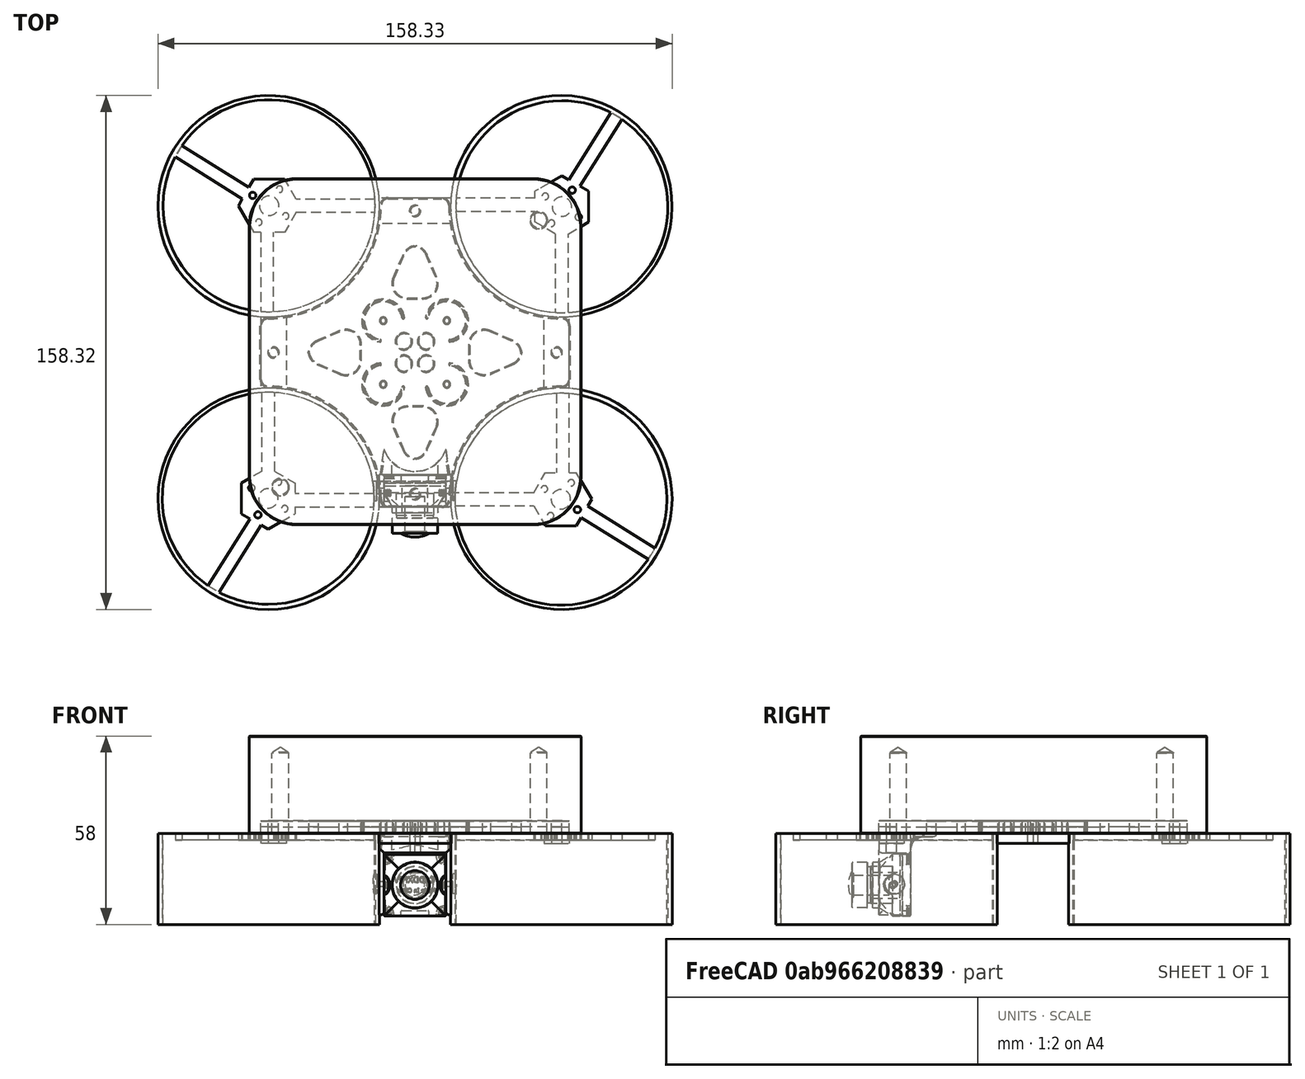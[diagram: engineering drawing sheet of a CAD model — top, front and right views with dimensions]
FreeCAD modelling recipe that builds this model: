
FCSTD DOCUMENT  (FreeCAD 1.1RUnknown)
Label: frame
License: All rights reserved
LicenseURL: http://en.wikipedia.org/wiki/All_rights_reserved
objects: Sketcher::SketchObject×17, PartDesign::SubShapeBinder×11, PartDesign::Pad×10, App::Point×5, PartDesign::Pocket×5, PartDesign::Body×5, PartDesign::Fillet×4, PartDesign::Mirrored×3, PartDesign::Hole×3, Part::Feature×2, Part::DatumPlane×2, Mesh::Feature×1, PartDesign::Chamfer×1, PartDesign::PolarPattern×1
note: 129 computed .brp shape members not serialized (recipe doc carries the construction recipe); baked Part::Feature solids carry a one-line shape summary decoded from their .brp

FEATURE [Mesh::Feature] bottom
FEATURE [Part::Feature] bottom001
  shape: bbox 94.96 x 95.06 x 2.45 mm, 2172 faces, 0 solids (baked)
FEATURE [Sketcher::SketchObject] Sketch
  ArcFitTolerance = 1e-06
  ExternalGeometry = -> [bottom001]
  ExternalTypes = [0,0,0,0,0,0,0,0,0,0,0,0,0,0,0,0,0,0,0]
  FullyConstrained = false
  MakeInternals = false
  sketch-geometry (35):
    g0: Circle [constr] CenterX=51.281 CenterY=31.7129 CenterZ=0 NormalX=0 NormalY=0 NormalZ=1 AngleXU=0 Radius=0.98
    g1: Circle [constr] CenterX=51.281 CenterY=51.3129 CenterZ=0 NormalX=0 NormalY=0 NormalZ=1 AngleXU=0 Radius=0.98
    g2: LineSegment [constr] StartX=-6 StartY=41.53 StartZ=0 EndX=88.962 EndY=41.53 EndZ=0
    g3: LineSegment [constr] StartX=88.962 StartY=49.8447 StartZ=0 EndX=88.962 EndY=33.2153 EndZ=0
    g4: LineSegment [constr] StartX=51.281 StartY=51.3129 StartZ=0 EndX=51.281 EndY=31.7129 EndZ=0
    g5: GeomPoint [constr] X=51.281 Y=41.53 Z=0
    g6: LineSegment [constr] StartX=51.281 StartY=89.06 StartZ=0 EndX=51.281 EndY=-8.95995 EndZ=0
    g7: LineSegment [constr] StartX=51.281 StartY=51.3129 StartZ=0 EndX=88.962 EndY=51.3129 EndZ=0
    g8: LineSegment [constr] StartX=51.281 StartY=31.7129 StartZ=0 EndX=88.962 EndY=31.7129 EndZ=0
    g9: LineSegment [constr] StartX=88.962 StartY=51.3129 StartZ=0 EndX=88.962 EndY=31.7129 EndZ=0
    g10: LineSegment [constr] StartX=41.481 StartY=89.06 StartZ=0 EndX=41.481 EndY=-13.0957 EndZ=0
    g11: GeomPoint [constr] X=41.481 Y=41.53 Z=0
    g12: LineSegment [constr] StartX=41.481 StartY=41.53 StartZ=0 EndX=88.962 EndY=41.53 EndZ=0
    g13: LineSegment [constr] StartX=88.962 StartY=41.53 StartZ=0 EndX=88.8951 EndY=48.4597 EndZ=0
    g14: LineSegment StartX=49.7388 StartY=89.06 StartZ=0 EndX=41.481 EndY=89.06 EndZ=0
    g15: LineSegment [constr] StartX=41.481 StartY=89.06 StartZ=0 EndX=41.481 EndY=41.53 EndZ=0
    g16: ArcOfCircle CenterX=49.7388 CenterY=86.7775 CenterZ=0 NormalX=0 NormalY=0 NormalZ=1 AngleXU=0 Radius=2.28248 StartAngle=6.28209 EndAngle=7.85398
    g17: LineSegment [constr] StartX=41.481 StartY=41.53 StartZ=0 EndX=69.212 EndY=69.261 EndZ=0
    g18: LineSegment [constr] StartX=41.481 StartY=41.53 StartZ=0 EndX=62.2347 EndY=62.2837 EndZ=0
    g19: ArcOfCircle CenterX=86.4023 CenterY=86.7373 CenterZ=0 NormalX=0 NormalY=0 NormalZ=1 AngleXU=0 Radius=34.381 StartAngle=3.1405 EndAngle=3.93287
    g20: Circle [constr] CenterX=41.481 CenterY=85.14 CenterZ=0 NormalX=0 NormalY=0 NormalZ=1 AngleXU=0 Radius=1.568
    g21: ArcOfCircle CenterX=41.4666 CenterY=85.1388 CenterZ=0 NormalX=0 NormalY=0 NormalZ=1 AngleXU=0 Radius=1.58246 StartAngle=4.72149 EndAngle=7.84488
    g22: LineSegment [constr] StartX=41.481 StartY=86.7212 StartZ=0 EndX=41.481 EndY=83.5564 EndZ=0
    g23: ArcOfCircle CenterX=41.0001 CenterY=69.8983 CenterZ=0 NormalX=0 NormalY=0 NormalZ=1 AngleXU=0 Radius=4.3878 StartAngle=0.322942 EndAngle=1.46098
    g24: LineSegment StartX=45.1611 StartY=71.2908 StartZ=0 EndX=47.9343 EndY=64.8997 EndZ=0
    g25: LineSegment StartX=43.7247 StartY=58.2122 StartZ=0 EndX=41.481 EndY=58.2122 EndZ=0
    g26: ArcOfCircle CenterX=43.8184 CenterY=62.7782 CenterZ=0 NormalX=0 NormalY=0 NormalZ=1 AngleXU=0 Radius=4.6305 StartAngle=5.73156 EndAngle=6.75912
    g27: ArcOfCircle CenterX=43.926 CenterY=62.712 CenterZ=0 NormalX=0 NormalY=0 NormalZ=1 AngleXU=0 Radius=4.50424 StartAngle=4.66769 EndAngle=5.73156
    g28: LineSegment StartX=41.481 StartY=41.53 StartZ=0 EndX=41.481 EndY=58.2122 EndZ=0
    g29: LineSegment StartX=41.481 StartY=74.2596 StartZ=0 EndX=41.481 EndY=83.5564 EndZ=0
    g30: LineSegment StartX=51.9654 StartY=52.0144 StartZ=0 EndX=62.2347 EndY=62.2837 EndZ=0
    g31: LineSegment StartX=41.481 StartY=86.7212 StartZ=0 EndX=41.481 EndY=89.06 EndZ=0
    g32: ArcOfCircle CenterX=51.281 CenterY=51.3129 CenterZ=0 NormalX=0 NormalY=0 NormalZ=1 AngleXU=0 Radius=0.98 StartAngle=1.5708 EndAngle=3.91468
    g33: LineSegment StartX=50.5796 StartY=50.6286 StartZ=0 EndX=41.481 EndY=41.53 EndZ=0
    g34: ArcOfCircle CenterX=51.281 CenterY=51.3129 CenterZ=0 NormalX=0 NormalY=0 NormalZ=1 AngleXU=0 Radius=0.98 StartAngle=0.797712 EndAngle=1.5708
  constraints (82):
    c: PointOnObject(g-3,g0)
    c: PointOnObject(g-4,g0)
    c: PointOnObject(g-9,g1)
    c: PointOnObject(g-8,g1)
    c: PointOnObject(g-7,g1)
    c: Diameter(g1) = 1.96
    c: Diameter(g0) = 1.96
    c: Coincident(g2,g-11)
    c: Horizontal(g2)
    c: Coincident(g3,g-14)
    c: Coincident(g3,g-14)
    c: PointOnObject(g2,g3)
    c: Coincident(g4,g1)
    c: Coincident(g4,g0)
    c: PointOnObject(g5,g2)
    c: PointOnObject(g5,g4)
    c: PointOnObject(g-5,g0)
    c: Vertical(g6)
    c: PointOnObject(g0,g6)
    c: Coincident(g7,g1)
    c: Horizontal(g7)
    c: Coincident(g8,g0)
    c: Horizontal(g8)
    c: Coincident(g9,g7)
    c: Coincident(g9,g8)
    c: Vertical(g9)
    c: PointOnObject(g3,g9)
    c: DistanceY(g0,g1) = 19.6
    c: Coincident(g10,g-16)
    c: Vertical(g10)
    c: Symmetric(g2,g2,g11)
    c: Coincident(g12,g11)
    c: Coincident(g12,g2)
    c: Coincident(g12,g13)
    c: Coincident(g14,g10)
    c: Coincident(g14,g15)
    c: Coincident(g15,g12)
    c: Tangent(g14,g16) = -1.5708
    c: Block(g16)
    c: Coincident(g17,g11)
    c: Angle(g12,g17) = 0.785398
    c: Coincident(g18,g11)
    c: PointOnObject(g18,g17)
    c: Tangent(g19,g16) = 1.5708
    c: Coincident(g18,g19)
    c: PointOnObject(g20,g15)
    c: PointOnObject(g-18,g20)
    c: PointOnObject(g-17,g20)
    c: PointOnObject(g21,g15)
    c: PointOnObject(g21,g15)
    c: Tangent(g21,g20)
    c: Coincident(g22,g21)
    c: Coincident(g22,g21)
    c: PointOnObject(g23,g15)
    c: Coincident(g23,g-19)
    c: Coincident(g24,g23)
    c: PointOnObject(g25,g15)
    c: Horizontal(g25)
    c: Coincident(g24,g-21)
    c: Coincident(g26,g24)
    c: Coincident(g27,g25)
    c: PointOnObject(g-20,g27)
    c: Tangent(g27,g26) = -1.5708
    c: Coincident(g28,g11)
    c: Coincident(g28,g25)
    c: Coincident(g29,g23)
    c: Coincident(g29,g21)
    c: Coincident(g30,g18)
    c: Coincident(g31,g21)
    c: Coincident(g31,g10)
    c: PointOnObject(g32,g6)
    c: PointOnObject(g32,g17)
    c: PointOnObject(g-7,g32)
    c: Equal(g32,g1)
    c: PointOnObject(g32,g1)
    c: Coincident(g33,g32)
    c: Coincident(g33,g11)
    c: PointOnObject(g30,g17)
    c: PointOnObject(g30,g1)
    c: Coincident(g34,g32)
    c: Coincident(g34,g30)
    c: Tangent(g34,g1)
FEATURE [App::Point] Origin001
  Role = Origin
FEATURE [PartDesign::SubShapeBinder] Binder
  BindCopyOnChange = 0
  BindMode = 0
  ClaimChildren = false
  Context = -> Body [Binder.]
  Fuse = false
  MakeFace = true
  OffsetFill = false
  OffsetIntersection = false
  OffsetJoinType = 0
  OffsetOpenResult = false
  PartialLoad = false
  Relative = true
  Support = -> [Sketch]
  _Version = 2
FEATURE [PartDesign::Pad] Pad
  Direction = (0,0,1)
  Length = 2
  Length2 = 10
  Profile = -> Binder
  Suppressed = false
  Type = 0
FEATURE [Sketcher::SketchObject] Sketch001
  ArcFitTolerance = 1e-06
  ExternalGeometry = -> [Binder]
  ExternalTypes = [0]
  FullyConstrained = false
  MakeInternals = false
  MapMode = 5
  Placement = pos=(0,0,2.5) rot=(0,0,1;0rad)
  sketch-geometry (6):
    g0: ArcOfCircle CenterX=51.281 CenterY=51.3129 CenterZ=0 NormalX=0 NormalY=0 NormalZ=1 AngleXU=0 Radius=6.5 StartAngle=0.787255 EndAngle=2.97698
    g1: ArcOfCircle CenterX=51.281 CenterY=51.3129 CenterZ=0 NormalX=0 NormalY=0 NormalZ=1 AngleXU=0 Radius=6 StartAngle=0.787409 EndAngle=2.97698
    g2: ArcOfCircle CenterX=45.1155 CenterY=52.3371 CenterZ=0 NormalX=0 NormalY=0 NormalZ=1 AngleXU=0 Radius=0.25 StartAngle=2.97698 EndAngle=6.11858
    g3: LineSegment StartX=55.5151 StartY=55.5641 StartZ=0 EndX=55.8687 EndY=55.9177 EndZ=0
    g4: ArcOfCircle CenterX=44.9101 CenterY=44.9591 CenterZ=0 NormalX=0 NormalY=0 NormalZ=1 AngleXU=0 Radius=2.5 StartAngle=0.785398 EndAngle=3.92699
    g5: LineSegment StartX=43.1424 StartY=43.1914 StartZ=0 EndX=46.6779 EndY=46.7269 EndZ=0
  constraints (16):
    c: Tangent(g2,g1) = 1.5708
    c: Tangent(g2,g0) = -1.5708
    c: Coincident(g3,g1)
    c: Coincident(g3,g0)
    c: Distance(g3,g3) = 0.5
    c: Coincident(g0,g1)
    c: Distance(g0,g1) = 6
    c: PointOnObject(g0,g-3)
    c: PointOnObject(g1,g-3)
    c: Coincident(g0,g-18)
    c: PointOnObject(g4,g-16)
    c: PointOnObject(g4,g-16)
    c: Radius(g4) = 2.5
    c: Angle(g4) = 3.14159
    c: Coincident(g5,g4)
    c: Coincident(g5,g4)
FEATURE [Sketcher::SketchObject] Sketch002
  ArcFitTolerance = 1e-06
  ExternalGeometry = -> [Binder]
  ExternalTypes = [0]
  FullyConstrained = true
  MakeInternals = false
  MapMode = 5
  Placement = pos=(0,0,2.5) rot=(0,0,1;0rad)
  sketch-geometry (2):
    g0: LineSegment [constr] StartX=41.481 StartY=41.53 StartZ=0 EndX=41.481 EndY=0 EndZ=0
    g1: LineSegment [constr] StartX=41.481 StartY=41.53 StartZ=0 EndX=0 EndY=41.53 EndZ=0
  constraints (8):
    c: Coincident(g0,g-16)
    c: PointOnObject(g0,g-1)
    c: Vertical(g0)
    c: DistanceY(g0,g0) = 41.53  'd'
    c: Coincident(g1,g0)
    c: PointOnObject(g1,g-2)
    c: Horizontal(g1)
    c: DistanceX(g1,g1) = 41.481  'd2'
FEATURE [Sketcher::SketchObject] Sketch003
  ArcFitTolerance = 1e-06
  AttachmentSupport = -> [XZ_Plane]
  ExternalGeometry = -> [Binder]
  ExternalTypes = [0]
  FullyConstrained = false
  MakeInternals = false
  MapMode = 5
  Placement = pos=(0,0,0) rot=(1,0,0;1.5708rad)
  sketch-geometry (1):
    g0: LineSegment StartX=41.481 StartY=0 StartZ=0 EndX=41.481 EndY=28.0906 EndZ=0
  constraints (2):
    c: Coincident(g0,g-3)
    c: Vertical(g0)
FEATURE [Sketcher::SketchObject] Sketch004
  ArcFitTolerance = 1e-06
  ExternalTypes = [0]
  FullyConstrained = false
  MakeInternals = false
  MapMode = 5
  Placement = pos=(41.481,41.53,-9.2e-15) rot=(1,0,0;1.5708rad)
  sketch-geometry (1):
    g0: LineSegment StartX=0 StartY=1.01324 StartZ=0 EndX=0 EndY=32.8937 EndZ=0
  constraints (2):
    c: PointOnObject(g0,g-2)
    c: PointOnObject(g0,g-2)
FEATURE [PartDesign::Pocket] Pocket
  BaseFeature = -> Pad
  Direction = (0,0,-1)
  Length = 5
  Length2 = 5
  Profile = -> Sketch001
  ReferenceAxis = -> Sketch001 [N_Axis]
  Suppressed = false
  Type = 1
FEATURE [PartDesign::Mirrored] Mirrored
  BaseFeature = -> Pocket
  MirrorPlane = -> Pocket [Face10]
  Originals = -> [Pocket]
  Suppressed = false
  TransformMode = 1
FEATURE [PartDesign::Mirrored] Mirrored001
  BaseFeature = -> Mirrored
  MirrorPlane = -> Mirrored [Face27]
  Originals = -> [Mirrored]
  Suppressed = false
  TransformMode = 1
FEATURE [PartDesign::Mirrored] Mirrored002
  BaseFeature = -> Mirrored001
  MirrorPlane = -> Mirrored001 [Face24]
  Originals = -> [Mirrored001]
  Refine = true
  Suppressed = false
  TransformMode = 1
FEATURE [PartDesign::Body] Body  label="bottom plate"
  AllowCompound = false
  Group = -> [Binder,Pad,Sketch001,Sketch002,Sketch003,Sketch004,Pocket,Mirrored,Mirrored001,Mirrored002]
  Origin = -> Origin
  Tip = -> Mirrored002
FEATURE [App::Point] Origin003
  Role = Origin
FEATURE [PartDesign::SubShapeBinder] Binder001
  BindCopyOnChange = 0
  BindMode = 0
  ClaimChildren = false
  Context = -> Body001 [Binder001.]
  Fuse = false
  MakeFace = true
  OffsetFill = false
  OffsetIntersection = false
  OffsetJoinType = 0
  OffsetOpenResult = false
  PartialLoad = false
  Relative = true
  Support = -> [Body]
  _Version = 2
FEATURE [Sketcher::SketchObject] Sketch005
  ArcFitTolerance = 1e-06
  AttachmentSupport = -> [XY_Plane001]
  ExternalTypes = [0]
  FullyConstrained = false
  MakeInternals = false
  MapMode = 5
  sketch-geometry (10):
    g0: LineSegment StartX=-9.59007 StartY=80.3505 StartZ=0 EndX=-9.59007 EndY=3.20138 EndZ=0
    g1: LineSegment StartX=5.13409 StartY=-11.5228 StartZ=0 EndX=77.9266 EndY=-11.5228 EndZ=0
    g2: LineSegment StartX=92.6508 StartY=3.20138 StartZ=0 EndX=92.6508 EndY=80.3505 EndZ=0
    g3: LineSegment StartX=77.9266 StartY=95.0747 StartZ=0 EndX=5.13409 EndY=95.0747 EndZ=0
    g4: ArcOfCircle CenterX=5.13409 CenterY=80.3505 CenterZ=0 NormalX=0 NormalY=0 NormalZ=1 AngleXU=0 Radius=14.7242 StartAngle=1.5708 EndAngle=3.14159
    g5: ArcOfCircle CenterX=5.13409 CenterY=3.20138 CenterZ=0 NormalX=0 NormalY=0 NormalZ=1 AngleXU=0 Radius=14.7242 StartAngle=3.14159 EndAngle=4.71239
    g6: ArcOfCircle CenterX=77.9266 CenterY=3.20138 CenterZ=0 NormalX=0 NormalY=0 NormalZ=1 AngleXU=0 Radius=14.7242 StartAngle=4.71239 EndAngle=6.28319
    g7: ArcOfCircle CenterX=77.9266 CenterY=80.3505 CenterZ=0 NormalX=0 NormalY=0 NormalZ=1 AngleXU=0 Radius=14.7242 StartAngle=1e-16 EndAngle=1.5708
    g8: GeomPoint [constr] X=-9.59007 Y=95.0747 Z=0
    g9: GeomPoint [constr] X=92.6508 Y=-11.5228 Z=0
  constraints (19):
    c: Tangent(g0,g4) = -1.5708
    c: Tangent(g0,g5) = -1.5708
    c: Tangent(g1,g5) = -1.5708
    c: Tangent(g1,g6) = -1.5708
    c: Tangent(g2,g6) = -1.5708
    c: Tangent(g2,g7) = -1.5708
    c: Tangent(g3,g7) = -1.5708
    c: Tangent(g3,g4) = -1.5708
    c: Vertical(g0)
    c: Vertical(g2)
    c: Horizontal(g1)
    c: Horizontal(g3)
    c: Equal(g4,g5)
    c: Equal(g5,g6)
    c: Equal(g6,g7)
    c: PointOnObject(g8,g0)
    c: PointOnObject(g8,g3)
    c: PointOnObject(g9,g1)
    c: PointOnObject(g9,g2)
FEATURE [PartDesign::SubShapeBinder] Binder002
  BindCopyOnChange = 0
  BindMode = 0
  ClaimChildren = false
  Context = -> Body001 [Binder002.]
  Fuse = false
  MakeFace = true
  Offset = -0.25
  OffsetFill = false
  OffsetIntersection = false
  OffsetJoinType = 0
  OffsetOpenResult = false
  PartialLoad = false
  Relative = true
  Support = -> [Body[Mirrored002.Face84]]
  _Version = 2
FEATURE [PartDesign::Pad] Pad001
  Direction = (0,0,1)
  Length = 10
  Length2 = 10
  Profile = -> Sketch005
  ReferenceAxis = -> Sketch005 [N_Axis]
  Reversed = true
  Suppressed = false
  Type = 0
FEATURE [PartDesign::Pad] Pad002
  BaseFeature = -> Pad001
  Direction = (0,0,1)
  Length = 10
  Length2 = 10
  Profile = -> Binder002
  Reversed = true
  Suppressed = false
  Type = 0
FEATURE [App::Point] Origin005
  Role = Origin
FEATURE [PartDesign::SubShapeBinder] Binder004
  BindCopyOnChange = 0
  BindMode = 0
  ClaimChildren = false
  Context = -> Body002 [Binder004.]
  Fuse = false
  MakeFace = true
  OffsetFill = false
  OffsetIntersection = false
  OffsetJoinType = 0
  OffsetOpenResult = false
  PartialLoad = false
  Relative = true
  Support = -> [Body001[Sketch005.]]
  _Version = 2
FEATURE [PartDesign::Pad] Pad003
  Direction = (0,0,1)
  Length = 30
  Length2 = 10
  Profile = -> Binder004
  Reversed = true
  Suppressed = false
  Type = 0
FEATURE [PartDesign::SubShapeBinder] Binder005
  BindCopyOnChange = 0
  BindMode = 0
  ClaimChildren = false
  Context = -> Body002 [Binder005.]
  Fuse = false
  MakeFace = true
  OffsetFill = false
  OffsetIntersection = false
  OffsetJoinType = 0
  OffsetOpenResult = false
  PartialLoad = false
  Relative = true
  Support = -> [Body[Mirrored002.Face5]]
  _Version = 2
FEATURE [PartDesign::Pocket] Pocket001
  BaseFeature = -> Pad003
  Direction = (0,1e-16,-1)
  Length = 4
  Length2 = 5
  Profile = -> Binder005
  Suppressed = false
  Type = 0
FEATURE [Sketcher::SketchObject] Sketch006
  ArcFitTolerance = 1e-06
  AttachmentSupport = -> [Pad002]
  ExternalTypes = [0]
  FullyConstrained = false
  MakeInternals = false
  MapMode = 5
  sketch-geometry (2):
    g0: Circle CenterX=0 CenterY=0 CenterZ=0 NormalX=0 NormalY=0 NormalZ=1 AngleXU=0 Radius=3.5
    g1: Circle CenterX=79.5784 CenterY=82.2311 CenterZ=0 NormalX=0 NormalY=0 NormalZ=1 AngleXU=0 Radius=3.5
  constraints (3):
    c: Coincident(g0,g-1)
    c: Equal(g1,g0)
    c: Diameter(g1) = 7
FEATURE [PartDesign::Pad] Pad004
  BaseFeature = -> Pad002
  Direction = (0,0,1)
  Length = 5
  Length2 = 10
  Profile = -> Sketch006
  ReferenceAxis = -> Sketch006 [N_Axis]
  Suppressed = false
  Type = 0
FEATURE [PartDesign::SubShapeBinder] Binder006
  BindCopyOnChange = 0
  BindMode = 0
  ClaimChildren = false
  Context = -> Body002 [Binder006.]
  Fuse = false
  MakeFace = true
  OffsetFill = false
  OffsetIntersection = false
  OffsetJoinType = 0
  OffsetOpenResult = false
  PartialLoad = false
  Relative = true
  Support = -> [Body001[Sketch006.]]
  _Version = 2
FEATURE [PartDesign::Hole] Hole
  BaseFeature = -> Pocket001
  CustomThreadClearance = 0
  Depth = 25
  DepthType = 0
  Diameter = 5.1
  DrillForDepth = false
  DrillPoint = 1
  DrillPointAngle = 118
  HoleCutCountersinkAngle = 90
  HoleCutCustomValues = false
  HoleCutDepth = 0
  HoleCutDiameter = 6.1
  HoleCutType = 0
  ModelThread = false
  Profile = -> Binder006
  Suppressed = false
  Tapered = false
  TaperedAngle = 90
  ThreadClass = 0
  ThreadDepth = 25
  ThreadDepthType = 0
  ThreadDirection = 0
  ThreadFit = 0
  ThreadSize = 0
  ThreadType = 0
  Threaded = false
  UseCustomThreadClearance = false
FEATURE [PartDesign::Chamfer] Chamfer
  Angle = 45
  Base = -> Hole [Edge131,Edge142]
  BaseFeature = -> Hole
  ChamferType = 0
  FlipDirection = false
  Size = 0.18
  Size2 = 1
  SupportTransform = false
  Suppressed = false
  UseAllEdges = true
FEATURE [PartDesign::Body] Body002
  AllowCompound = false
  Group = -> [Binder004,Pad003,Binder005,Pocket001,Binder006,Hole,Chamfer]
  Origin = -> Origin004
  Placement = pos=(0,-120.18,43.09) rot=(1,0,0;3.14159rad)
  Tip = -> Chamfer
FEATURE [PartDesign::Fillet] Fillet
  Base = -> Pad002 [Face31,Face138,Face139,Face137,Face136,Face4]
  BaseFeature = -> Pad002
  Radius = 0.18
  SupportTransform = false
  Suppressed = false
  UseAllEdges = false
FEATURE [PartDesign::Body] Body001  label="Body"
  AllowCompound = false
  Group = -> [Binder001,Sketch005,Binder002,Pad001,Pad002,Sketch006,Pad004,Fillet]
  Origin = -> Origin002
  Tip = -> Fillet
FEATURE [App::Point] Origin007
  Role = Origin
FEATURE [PartDesign::SubShapeBinder] Binder007
  BindCopyOnChange = 0
  BindMode = 0
  ClaimChildren = false
  Context = -> Body003 [Binder007.]
  Fuse = false
  MakeFace = true
  OffsetFill = false
  OffsetIntersection = false
  OffsetJoinType = 0
  OffsetOpenResult = false
  PartialLoad = false
  Relative = true
  Support = -> [Body]
  _Version = 2
FEATURE [Sketcher::SketchObject] Sketch007
  ArcFitTolerance = 1e-06
  AttachmentSupport = -> [XY_Plane003]
  ExternalGeometry = -> [Binder007]
  ExternalTypes = [0,0,0,0,0,0]
  FullyConstrained = true
  MakeInternals = false
  MapMode = 5
  sketch-geometry (5):
    g0: LineSegment [constr] StartX=86.4023 StartY=-3.67734 StartZ=0 EndX=86.6883 EndY=-3.39127 EndZ=0
    g1: GeomPoint [constr] X=86.5453 Y=-3.53431 Z=0
    g2: Circle [constr] CenterX=86.5453 CenterY=-3.53431 CenterZ=0 NormalX=0 NormalY=0 NormalZ=1 AngleXU=0 Radius=31.75
    g3: Circle CenterX=86.5453 CenterY=-3.53431 CenterZ=0 NormalX=0 NormalY=0 NormalZ=1 AngleXU=0 Radius=34.1
    g4: Circle CenterX=86.4023 CenterY=-3.67734 CenterZ=0 NormalX=0 NormalY=0 NormalZ=1 AngleXU=0 Radius=32.6477
  constraints (9):
    c: Coincident(g0,g-7)
    c: Coincident(g0,g-8)
    c: Symmetric(g0,g0,g1)
    c: Coincident(g2,g1)
    c: Diameter(g2) = 63.5
    c: Coincident(g3,g1)
    c: Distance(g3,g2) = 2.35
    c: Coincident(g4,g0)
    c: Distance(g4,g3) = 1.25
FEATURE [PartDesign::Pad] Pad005
  Direction = (0,0,1)
  Length = 0
  Length2 = 28
  Profile = -> Sketch007
  ReferenceAxis = -> Sketch007 [N_Axis]
  Suppressed = false
  Type = 4
FEATURE [Sketcher::SketchObject] Sketch008
  ArcFitTolerance = 1e-06
  AttachmentSupport = -> [Pad005]
  ExternalGeometry = -> [Binder007,Pad005]
  ExternalTypes = [0,0,0,0,0,0]
  FullyConstrained = true
  MakeInternals = false
  MapMode = 5
  sketch-geometry (12):
    g0: LineSegment StartX=89.011 StartY=28.866 StartZ=0 EndX=89.011 EndY=41.53 EndZ=0
    g1: LineSegment [constr] StartX=89.011 StartY=41.53 StartZ=0 EndX=81.1685 EndY=41.53 EndZ=0
    g2: LineSegment StartX=81.1685 StartY=41.53 StartZ=0 EndX=81.1685 EndY=29.8314 EndZ=0
    g3: ArcOfCircle CenterX=85.0898 CenterY=41.5444 CenterZ=0 NormalX=0 NormalY=0 NormalZ=1 AngleXU=0 Radius=1.58246 StartAngle=3.15069 EndAngle=6.27408
    g4: LineSegment StartX=81.1685 StartY=41.53 StartZ=0 EndX=83.5074 EndY=41.53 EndZ=0
    g5: LineSegment StartX=86.6722 StartY=41.53 StartZ=0 EndX=89.011 EndY=41.53 EndZ=0
    g6: LineSegment StartX=81.1685 StartY=29.8314 StartZ=0 EndX=89.011 EndY=28.866 EndZ=0
    g7: LineSegment StartX=41.481 StartY=-3.66116 StartZ=0 EndX=41.481 EndY=-6 EndZ=0
    g8: LineSegment StartX=41.481 StartY=-6 StartZ=0 EndX=53.8373 EndY=-6 EndZ=0
    g9: LineSegment StartX=53.8373 StartY=-6 StartZ=0 EndX=52.8719 EndY=1.84248 EndZ=0
    g10: LineSegment StartX=41.481 StartY=-0.496368 StartZ=0 EndX=41.481 EndY=1.84248 EndZ=0
    g11: LineSegment StartX=41.481 StartY=1.84248 StartZ=0 EndX=52.8719 EndY=1.84248 EndZ=0
  constraints (32):
    c: Coincident(g0,g1)
    c: Coincident(g1,g2)
    c: Horizontal(g1)
    c: Vertical(g0)
    c: Vertical(g2)
    c: PointOnObject(g-5,g0)
    c: PointOnObject(g-4,g1)
    c: Tangent(g3,g-4) = -1.5708
    c: Coincident(g3,g-4)
    c: Coincident(g4,g1)
    c: Coincident(g4,g-4)
    c: Coincident(g5,g3)
    c: Coincident(g5,g0)
    c: Coincident(g6,g2)
    c: Coincident(g6,g0)
    c: Coincident(g7,g-6)
    c: Vertical(g7)
    c: Coincident(g8,g7)
    c: Horizontal(g8)
    c: Coincident(g9,g8)
    c: Equal(g9,g6)
    c: Coincident(g10,g-6)
    c: Vertical(g10)
    c: Equal(g5,g7)
    c: Equal(g4,g10)
    c: Equal(g10,g7)
    c: Coincident(g11,g10)
    c: Coincident(g11,g9)
    c: Horizontal(g11)
    c: PointOnObject(g8,g-7)
    c: PointOnObject(g9,g-8)
    c: PointOnObject(g0,g-7)
FEATURE [PartDesign::Pad] Pad006
  BaseFeature = -> Pad005
  Direction = (0,0,1)
  Length = 3
  Length2 = 10
  Profile = -> Sketch008
  ReferenceAxis = -> Sketch008 [N_Axis]
  Reversed = true
  Suppressed = false
  Type = 0
FEATURE [Sketcher::SketchObject] Sketch009
  ArcFitTolerance = 1e-06
  AttachmentSupport = -> [XY_Plane003]
  ExternalGeometry = -> [Sketch008,Pad006]
  ExternalTypes = [0,0,0,0]
  FullyConstrained = false
  MakeInternals = false
  MapMode = 5
  sketch-geometry (36):
    g0: LineSegment [constr] StartX=91.1523 StartY=4.5499 StartZ=0 EndX=81.6523 EndY=4.5499 EndZ=0
    g1: LineSegment [constr] StartX=81.6523 StartY=4.5499 StartZ=0 EndX=76.9023 EndY=-3.67734 EndZ=0
    g2: LineSegment [constr] StartX=76.9023 StartY=-3.67734 StartZ=0 EndX=81.6523 EndY=-11.9046 EndZ=0
    g3: LineSegment StartX=81.6523 StartY=-11.9046 StartZ=0 EndX=91.1523 EndY=-11.9046 EndZ=0
    g4: LineSegment [constr] StartX=91.1523 StartY=-11.9046 StartZ=0 EndX=95.9023 EndY=-3.67734 EndZ=0
    g5: LineSegment StartX=95.9023 StartY=-3.67734 StartZ=0 EndX=91.1523 EndY=4.5499 EndZ=0
    g6: Circle [constr] CenterX=86.4023 CenterY=-3.67734 CenterZ=0 NormalX=0 NormalY=0 NormalZ=1 AngleXU=0 Radius=9.5
    g7: LineSegment [constr] StartX=95.9023 StartY=-3.67734 StartZ=0 EndX=76.9023 EndY=-3.67734 EndZ=0
    g8: LineSegment StartX=78.057 StartY=-1.67734 StartZ=0 EndX=53.8159 EndY=-1.67734 EndZ=0
    g9: LineSegment [constr] StartX=53.8159 StartY=-1.67734 StartZ=0 EndX=53.8159 EndY=-5.67734 EndZ=0
    g10: LineSegment StartX=53.8159 StartY=-5.67734 StartZ=0 EndX=78.057 EndY=-5.67734 EndZ=0
    g11: LineSegment [constr] StartX=78.057 StartY=-5.67734 StartZ=0 EndX=78.057 EndY=-1.67734 EndZ=0
    g12: LineSegment StartX=78.057 StartY=-1.67734 StartZ=0 EndX=81.6523 EndY=4.5499 EndZ=0
    g13: LineSegment StartX=78.057 StartY=-5.67734 StartZ=0 EndX=81.6523 EndY=-11.9046 EndZ=0
    g14: ArcOfCircle CenterX=55.6667 CenterY=-3.67734 CenterZ=0 NormalX=0 NormalY=0 NormalZ=1 AngleXU=0 Radius=2.725 StartAngle=2.31748 EndAngle=3.9657
    g15: LineSegment StartX=92.6685 StartY=-9.27845 StartZ=0 EndX=113.29 EndY=-22.1957 EndZ=0
    g16: LineSegment StartX=94.6685 StartY=-5.81435 StartZ=0 EndX=115.352 EndY=-18.7704 EndZ=0
    g17: ArcOfCircle CenterX=112.734 CenterY=-19.528 CenterZ=0 NormalX=0 NormalY=0 NormalZ=1 AngleXU=0 Radius=2.725 StartAngle=4.91775 EndAngle=6.56491
    g18: LineSegment StartX=91.1523 StartY=-11.9046 StartZ=0 EndX=92.6685 EndY=-9.27845 EndZ=0
    g19: LineSegment StartX=94.6685 StartY=-5.81435 StartZ=0 EndX=95.9023 EndY=-3.67734 EndZ=0
    g20: LineSegment [constr] StartX=85.011 StartY=4.5499 StartZ=0 EndX=89.011 EndY=4.5499 EndZ=0
    g21: LineSegment StartX=89.011 StartY=4.5499 StartZ=0 EndX=89.011 EndY=28.866 EndZ=0
    g22: LineSegment [constr] StartX=89.011 StartY=28.866 StartZ=0 EndX=85.011 EndY=28.866 EndZ=0
    g23: LineSegment StartX=85.011 StartY=28.866 StartZ=0 EndX=85.011 EndY=4.5499 EndZ=0
    g24: LineSegment StartX=81.6523 StartY=4.5499 StartZ=0 EndX=85.011 EndY=4.5499 EndZ=0
    g25: LineSegment StartX=89.011 StartY=4.5499 StartZ=0 EndX=91.1523 EndY=4.5499 EndZ=0
    g26: LineSegment [constr] StartX=89.011 StartY=28.866 StartZ=0 EndX=89.011 EndY=28.866 EndZ=0
    g27: ArcOfCircle CenterX=87.011 CenterY=27.0151 CenterZ=0 NormalX=0 NormalY=0 NormalZ=1 AngleXU=0 Radius=2.725 StartAngle=0.746684 EndAngle=2.39491
    g28: LineSegment [constr] StartX=86.4023 StartY=-3.67734 StartZ=0 EndX=114.07 EndY=-21.0084 EndZ=0
    g29: Circle CenterX=81.3175 CenterY=-0.492235 CenterZ=0 NormalX=0 NormalY=0 NormalZ=1 AngleXU=0 Radius=1
    g30: Circle CenterX=89.5874 CenterY=1.40744 CenterZ=0 NormalX=0 NormalY=0 NormalZ=1 AngleXU=0 Radius=1
    g31: Circle CenterX=91.4871 CenterY=-6.86245 CenterZ=0 NormalX=0 NormalY=0 NormalZ=1 AngleXU=0 Radius=1
    g32: Circle CenterX=83.2172 CenterY=-8.76213 CenterZ=0 NormalX=0 NormalY=0 NormalZ=1 AngleXU=0 Radius=1
    g33: LineSegment [constr] StartX=81.3175 StartY=-0.492235 StartZ=0 EndX=91.4871 EndY=-6.86245 EndZ=0
    g34: LineSegment [constr] StartX=89.5874 StartY=1.40744 StartZ=0 EndX=83.2172 EndY=-8.76213 EndZ=0
    g35: Circle CenterX=86.4023 CenterY=-3.67734 CenterZ=0 NormalX=0 NormalY=0 NormalZ=1 AngleXU=0 Radius=3
  constraints (92):
    c: Coincident(g0,g1)
    c: Coincident(g1,g2)
    c: Coincident(g2,g3)
    c: Coincident(g3,g4)
    c: Coincident(g4,g5)
    c: Coincident(g5,g0)
    c: Equal(g0, g1-g5) x5
    c: PointOnObject(g0,g6)
    c: PointOnObject(g1,g6)
    c: PointOnObject(g2,g6)
    c: PointOnObject(g3,g6)
    c: PointOnObject(g4,g6)
    c: PointOnObject(g5,g6)
    c: Coincident(g6,g-4)
    c: Diameter(g6) = 19
    c: Horizontal(g3)
    c: Coincident(g7,g4)
    c: PointOnObject(g7,g1)
    c: Horizontal(g7)
    c: Coincident(g8,g9)
    c: Coincident(g9,g10)
    c: Coincident(g10,g11)
    c: Coincident(g11,g8)
    c: Horizontal(g8)
    c: Horizontal(g10)
    c: Vertical(g9)
    c: Vertical(g11)
    c: PointOnObject(g8,g1)
    c: PointOnObject(g10,g2)
    c: Coincident(g12,g8)
    c: Coincident(g12,g0)
    c: Coincident(g13,g10)
    c: Coincident(g13,g2)
    c: PointOnObject(g8,g-5)
    c: DistanceY(g9,g9) = 4
    c: Coincident(g14,g8)
    c: Coincident(g14,g9)
    c: PointOnObject(g15,g4)
    c: PointOnObject(g15,g-5)
    c: PointOnObject(g16,g4)
    c: PointOnObject(g16,g-5)
    c: Coincident(g17,g16)
    c: Coincident(g17,g15)
    c: Coincident(g18,g3)
    c: Coincident(g18,g15)
    c: Coincident(g19,g16)
    c: Coincident(g19,g4)
    c: Equal(g17,g14)
    c: Radius(g14) = 2.725
    c: Parallel(g15,g16)
    c: Distance(g15,g16) = 4
    c: Coincident(g20,g21)
    c: Coincident(g21,g22)
    c: Coincident(g22,g23)
    c: Coincident(g23,g20)
    c: Horizontal(g20)
    c: Horizontal(g22)
    c: Vertical(g21)
    c: Vertical(g23)
    c: PointOnObject(g20,g0)
    c: PointOnObject(g21,g-4)
    c: DistanceX(g22,g22) = 4
    c: Coincident(g24,g0)
    c: Coincident(g24,g20)
    c: Coincident(g25,g20)
    c: Coincident(g25,g0)
    c: Coincident(g26,g-6)
    c: Coincident(g26,g21)
    c: Vertical(g26)
    c: Coincident(g27,g22)
    c: Coincident(g27,g21)
    c: Equal(g27,g17)
    c: Coincident(g28,g6)
    c: PointOnObject(g28,g-5)
    c: Parallel(g15,g28)
    c: Equal(g32,g31)
    c: Equal(g31,g30)
    c: Equal(g30,g29)
    c: Diameter(g29) = 2
    c: Coincident(g33,g29)
    c: Coincident(g33,g31)
    c: Distance(g33,g33) = 12
    c: Coincident(g34,g30)
    c: Coincident(g32,g34)
    c: Distance(g34,g34) = 12
    c: Symmetric(g32,g30,g33)
    c: Symmetric(g31,g29,g34)
    c: PointOnObject(g31,g28)
    c: PointOnObject(g6,g34)
    c: PointOnObject(g6,g33)
    c: Coincident(g35,g6)
    c: Diameter(g35) = 6
FEATURE [PartDesign::Pad] Pad007
  BaseFeature = -> Pad006
  Direction = (0,0,1)
  Length = 2
  Length2 = 10
  Profile = -> Sketch009
  ReferenceAxis = -> Sketch009 [N_Axis]
  Refine = true
  Reversed = true
  Suppressed = false
  Type = 0
FEATURE [PartDesign::SubShapeBinder] Binder008
  BindCopyOnChange = 0
  BindMode = 0
  ClaimChildren = false
  Context = -> Body003 [Binder008.]
  Fuse = false
  MakeFace = true
  OffsetFill = false
  OffsetIntersection = false
  OffsetJoinType = 0
  OffsetOpenResult = false
  PartialLoad = false
  Relative = true
  Support = -> [Body[Sketch004.]]
  _Version = 2
FEATURE [PartDesign::PolarPattern] PolarPattern
  Angle = 360
  Axis = -> Binder008 [Edge1]
  BaseFeature = -> Pad007
  Mode = 0
  Occurrences = 4
  Offset = 120
  Originals = -> [Pad007]
  Refine = true
  Suppressed = false
  TransformMode = 1
FEATURE [App::Point] Origin009
  Role = Origin
FEATURE [PartDesign::SubShapeBinder] Binder009
  BindCopyOnChange = 0
  BindMode = 0
  ClaimChildren = false
  Context = -> Body004 [Binder009.]
  Fuse = false
  MakeFace = true
  OffsetFill = false
  OffsetIntersection = false
  OffsetJoinType = 0
  OffsetOpenResult = false
  PartialLoad = false
  Relative = true
  Support = -> [Body]
  _Version = 2
FEATURE [Sketcher::SketchObject] Sketch010
  ArcFitTolerance = 1e-06
  AttachmentSupport = -> [XY_Plane004]
  ExternalGeometry = -> [Binder009]
  ExternalTypes = [0,0,0,0,0,0,0,0,0,0,0,0,0,0,0,0]
  FullyConstrained = false
  MakeInternals = false
  MapMode = 5
  sketch-geometry (7):
    g0: LineSegment StartX=30.4666 StartY=1.84248 StartZ=0 EndX=52.4666 EndY=1.84248 EndZ=0
    g1: LineSegment [constr] StartX=31.9666 StartY=34.7471 StartZ=0 EndX=53.9091 EndY=34.7471 EndZ=0
    g2: LineSegment [constr] StartX=41.4666 StartY=1.84248 StartZ=0 EndX=41.4666 EndY=34.7462 EndZ=0
    g3: ArcOfCircle CenterX=41.4666 CenterY=14.8425 CenterZ=0 NormalX=0 NormalY=0 NormalZ=1 AngleXU=0 Radius=10 StartAngle=3.46724 EndAngle=5.95754
    g4: GeomPoint X=41.4666 Y=4.84248 Z=0
    g5: LineSegment StartX=30.4666 StartY=1.84248 StartZ=0 EndX=31.9922 EndY=11.6432 EndZ=0
    g6: LineSegment StartX=50.941 StartY=11.6432 StartZ=0 EndX=52.4666 EndY=1.84248 EndZ=0
  constraints (14):
    c: Horizontal(g0)
    c: Horizontal(g1)
    c: Symmetric(g0,g0,g2)
    c: PointOnObject(g-3,g2)
    c: Vertical(g2)
    c: DistanceX(g0,g0) = 22
    c: PointOnObject(g4,g3)
    c: Distance(g4,g0) = 3
    c: Radius(g3) = 10
    c: Symmetric(g3,g3,g2)
    c: Coincident(g5,g0)
    c: Coincident(g5,g3)
    c: Coincident(g6,g3)
    c: Coincident(g6,g0)
FEATURE [PartDesign::SubShapeBinder] Binder010
  BindCopyOnChange = 0
  BindMode = 0
  ClaimChildren = false
  Context = -> Body004 [Binder010.]
  Fuse = false
  MakeFace = true
  OffsetFill = false
  OffsetIntersection = false
  OffsetJoinType = 0
  OffsetOpenResult = false
  PartialLoad = false
  Relative = true
  Support = -> [Body003]
  _Version = 2
FEATURE [PartDesign::Pad] Pad008
  Direction = (0,0,1)
  Length = 1
  Length2 = 10
  Profile = -> Sketch010
  ReferenceAxis = -> Sketch010 [N_Axis]
  Reversed = true
  Suppressed = false
  Type = 0
FEATURE [Part::DatumPlane] Plane
  AttachmentSupport = -> [Pad008,Origin008]
  MapMode = 6
  Placement = pos=(52.4666,1.84248,-1) rot=(0.57735,-0.57735,0.57735;4.18879rad)
FEATURE [Sketcher::SketchObject] Sketch011
  ArcFitTolerance = 1e-06
  AttachmentSupport = -> [Plane]
  ExternalGeometry = -> [Binder010]
  ExternalTypes = [0,0,0]
  FullyConstrained = true
  MakeInternals = false
  MapMode = 5
  Placement = pos=(52.4666,1.84248,-1) rot=(0.57735,-0.57735,0.57735;4.18879rad)
  sketch-geometry (5):
    g0: LineSegment StartX=1.33471 StartY=21 StartZ=0 EndX=-116.852 EndY=21 EndZ=0
    g1: LineSegment StartX=-116.852 StartY=21 StartZ=0 EndX=-116.852 EndY=27 EndZ=0
    g2: LineSegment StartX=-116.852 StartY=27 StartZ=0 EndX=-118.852 EndY=27 EndZ=0
    g3: LineSegment StartX=-50.6518 StartY=27 StartZ=0 EndX=1.33471 EndY=-1 EndZ=0
    g4: LineSegment StartX=1.33471 StartY=-1 StartZ=0 EndX=1.33471 EndY=21 EndZ=0
  constraints (13):
    c: Horizontal(g0)
    c: Coincident(g1,g0)
    c: Vertical(g1)
    c: Coincident(g2,g1)
    c: Horizontal(g2)
    c: Coincident(g3,g-3)
    c: Coincident(g4,g3)
    c: Vertical(g4)
    c: Coincident(g0,g4)
    c: DistanceY(g4,g4) = 22
    c: Distance(g2,g2) = 2
    c: Coincident(g3,g-5)
    c: Coincident(g2,g-3)
FEATURE [PartDesign::Pad] Pad009
  BaseFeature = -> Pad008
  Direction = (1,0,0)
  Length = 22
  Length2 = 10
  Profile = -> Sketch011
  ReferenceAxis = -> Sketch011 [N_Axis]
  Reversed = true
  Suppressed = false
  Type = 0
FEATURE [Part::Feature] Part__Feature  label="Caddx Nebula Pro v18"
  Placement = pos=(41.46,-5.81,-15.87) rot=(0.57735,0.57735,0.57735;2.0944rad)
  shape: bbox 19.46 x 19.32 x 19.13 mm, 1092 faces, 9 solids (baked)
FEATURE [Part::DatumPlane] Plane001
  AttachmentSupport = -> [Origin006,PolarPattern]
  MapMode = 6
  Placement = pos=(0,-6,-3) rot=(0.57735,-0.57735,0.57735;4.18879rad)
FEATURE [Sketcher::SketchObject] Sketch015
  ArcFitTolerance = 1e-06
  AttachmentOffset = pos=(0,0,28.4) rot=(0,0,1;0rad)
  AttachmentSupport = -> [Plane001]
  ExternalGeometry = -> [PolarPattern]
  ExternalTypes = [0,0,0]
  FullyConstrained = false
  MakeInternals = false
  MapMode = 5
  Placement = pos=(28.4,-6,-3) rot=(0.57735,-0.57735,0.57735;4.18879rad)
  expr: Constraints[2] = 12.5 mm
  expr: Constraints[6] = 9.842 mm / 2
  sketch-geometry (3):
    g0: LineSegment [constr] StartX=-3.92124 StartY=-1.29e-14 StartZ=0 EndX=-3.92124 EndY=12.5 EndZ=0
    g1: Circle CenterX=-4.921 CenterY=12.5335 CenterZ=0 NormalX=0 NormalY=0 NormalZ=1 AngleXU=0 Radius=2.5
    g2: LineSegment [constr] StartX=-36.4764 StartY=2.2e-15 StartZ=0 EndX=5.75841 EndY=2.2e-15 EndZ=0
  constraints (7):
    c: Symmetric(g-3,g-3,g0)
    c: Vertical(g0)
    c: DistanceY(g0,g0) = 12.5
    c: Diameter(g1) = 5
    c: Coincident(g2,g-4)
    c: Horizontal(g2)
    c: DistanceX(g1,g-1) = 4.921
FEATURE [Sketcher::SketchObject] Sketch016
  ArcFitTolerance = 1e-06
  AttachmentSupport = -> [Pad009]
  ExternalGeometry = -> [Pad009]
  ExternalTypes = [0]
  FullyConstrained = true
  MakeInternals = false
  MapMode = 5
  Placement = pos=(0,-6,0) rot=(1,0,0;1.5708rad)
  sketch-geometry (6):
    g0: LineSegment StartX=31.9666 StartY=-25 StartZ=0 EndX=50.9666 EndY=-25 EndZ=0
    g1: LineSegment [constr] StartX=50.9666 StartY=-25 StartZ=0 EndX=52.4666 EndY=-25 EndZ=0
    g2: LineSegment [constr] StartX=31.9666 StartY=-25 StartZ=0 EndX=30.4666 EndY=-25 EndZ=0
    g3: LineSegment StartX=31.9666 StartY=-25 StartZ=0 EndX=31.9666 EndY=-6 EndZ=0
    g4: LineSegment StartX=50.9666 StartY=-25 StartZ=0 EndX=50.9666 EndY=-6 EndZ=0
    g5: LineSegment StartX=31.9666 StartY=-6 StartZ=0 EndX=50.9666 EndY=-6 EndZ=0
  constraints (16):
    c: PointOnObject(g0,g-3)
    c: PointOnObject(g0,g-3)
    c: DistanceX(g0,g0) = 19
    c: Coincident(g1,g0)
    c: Coincident(g1,g-3)
    c: Coincident(g2,g0)
    c: Coincident(g2,g-3)
    c: Equal(g2,g1)
    c: Coincident(g3,g0)
    c: Vertical(g3)
    c: Coincident(g4,g0)
    c: Vertical(g4)
    c: Equal(g3,g4)
    c: DistanceY(g4,g4) = 19
    c: Coincident(g5,g3)
    c: Coincident(g5,g4)
FEATURE [PartDesign::Pocket] Pocket006
  BaseFeature = -> Pad009
  Direction = (0,1,-2e-16)
  Length = 5
  Length2 = 5
  Profile = -> Sketch016
  ReferenceAxis = -> Sketch016 [N_Axis]
  Suppressed = false
  Type = 1
FEATURE [Sketcher::SketchObject] Sketch017
  ArcFitTolerance = 1e-06
  AttachmentSupport = -> [Pocket006]
  ExternalGeometry = -> [Pocket006]
  ExternalTypes = [0,0]
  FullyConstrained = true
  MakeInternals = false
  MapMode = 5
  Placement = pos=(31.9666,0,0) rot=(0.57735,0.57735,0.57735;2.0944rad)
  sketch-geometry (3):
    g0: LineSegment [constr] StartX=-1.07876 StartY=-25 StartZ=0 EndX=-1.07876 EndY=-15.5 EndZ=0
    g1: LineSegment [constr] StartX=-1.07876 StartY=-15.5 StartZ=0 EndX=-1.07876 EndY=-6 EndZ=0
    g2: Circle CenterX=-1.07876 CenterY=-15.5 CenterZ=0 NormalX=0 NormalY=0 NormalZ=1 AngleXU=0 Radius=0.75
  constraints (10):
    c: Symmetric(g-6,g-6,g0)
    c: Vertical(g0)
    c: Coincident(g1,g0)
    c: Symmetric(g-4,g-4,g1)
    c: Equal(g1,g0)
    c: Coincident(g2,g0)
    c: Diameter(g2) = 1.5
    c: DistanceY(g0,g1) = 9.5
    c: Distance(g-4,g0) = 4.92124  'd'
    c: DistanceX(g-4,g-5) = 9.84248
FEATURE [PartDesign::Pocket] Pocket007
  BaseFeature = -> Pocket006
  Direction = (-1,0,0)
  Length = 5
  Length2 = 5
  Midplane = true
  Profile = -> Sketch017
  ReferenceAxis = -> Sketch017 [N_Axis]
  Suppressed = false
  Type = 1
FEATURE [Sketcher::SketchObject] Sketch018
  ArcFitTolerance = 1e-06
  AttachmentSupport = -> [Pocket007]
  ExternalGeometry = -> [Binder009]
  ExternalTypes = [0,0]
  FullyConstrained = true
  MakeInternals = false
  MapMode = 5
  Placement = pos=(8e-16,-1.3e-15,-6) rot=(1,0,0;3.14159rad)
FEATURE [PartDesign::Pocket] Pocket008
  BaseFeature = -> Pocket007
  Direction = (0,0,1)
  Length = 5
  Length2 = 5
  Profile = -> Sketch018
  ReferenceAxis = -> Sketch018 [N_Axis]
  Suppressed = false
  Type = 1
FEATURE [PartDesign::Fillet] Fillet001
  Base = -> Pocket008 [Edge23]
  BaseFeature = -> Pocket008
  Radius = 4
  SupportTransform = false
  Suppressed = false
  UseAllEdges = false
FEATURE [PartDesign::Fillet] Fillet002
  Base = -> Fillet001 [Edge49,Edge43,Edge40,Edge50,Edge35]
  BaseFeature = -> Fillet001
  Radius = 1
  SupportTransform = false
  Suppressed = false
  UseAllEdges = false
FEATURE [Sketcher::SketchObject] Sketch019
  ArcFitTolerance = 1e-06
  ExternalGeometry = -> [Part__Feature]
  ExternalTypes = [0,0]
  FullyConstrained = false
  MakeInternals = false
  sketch-geometry (6):
    g0: LineSegment StartX=37.0227 StartY=-14.21 StartZ=0 EndX=41.4954 EndY=-14.21 EndZ=0
    g1: LineSegment [constr] StartX=41.4954 StartY=-14.21 StartZ=0 EndX=41.4954 EndY=-85.397 EndZ=0
    g2: LineSegment StartX=0 StartY=-44.8149 StartZ=0 EndX=37.0227 EndY=-14.21 EndZ=0
    g3: LineSegment [constr] StartX=41.4954 StartY=-2.07876 StartZ=0 EndX=41.4954 EndY=-14.21 EndZ=0
    g4: LineSegment StartX=45.8973 StartY=-14.21 StartZ=0 EndX=82.9908 EndY=-44.8149 EndZ=0
    g5: LineSegment [constr] StartX=0 StartY=-44.8149 StartZ=0 EndX=82.9908 EndY=-44.8149 EndZ=0
  constraints (17):
    c: Horizontal(g0)
    c: Coincident(g1,g0)
    c: Vertical(g1)
    c: PointOnObject(g2,g-2)
    c: Coincident(g2,g0)
    c: Tangent(g2,g-12)
    c: Angle(g2,g1) = 0.880013
    c: Coincident(g3,g-110)
    c: Coincident(g3,g0)
    c: Vertical(g3)
    c: Coincident(g0,g-131)
    c: Coincident(g4,g-131)
    c: Symmetric(g4,g2,g1)
    c: Angle(g1,g4) = 0.880951
    c: Angle(g2,g4) = 1.76096
    c: Coincident(g5,g2)
    c: Coincident(g5,g4)
FEATURE [PartDesign::Fillet] Fillet003
  Base = -> Fillet002 [Edge39,Edge60,Edge6,Edge4,Edge8]
  BaseFeature = -> Fillet002
  Radius = 0.5
  SupportTransform = false
  Suppressed = false
  UseAllEdges = false
FEATURE [PartDesign::Body] Body004  label="camera mount"
  AllowCompound = false
  Group = -> [Binder009,Sketch010,Binder010,Pad008,Plane,Sketch011,Pad009,Sketch016,Pocket006,Sketch017,Pocket007,Sketch018,Pocket008,Fillet001,Fillet002,Fillet003]
  Origin = -> Origin008
  Tip = -> Fillet003
FEATURE [PartDesign::Hole] Hole001
  BaseFeature = -> PolarPattern
  CustomThreadClearance = 0
  Depth = 15.822
  DepthType = 0
  Diameter = 1.8
  DrillForDepth = false
  DrillPoint = 1
  DrillPointAngle = 118
  HoleCutCountersinkAngle = 90
  HoleCutCustomValues = false
  HoleCutDepth = 1.3
  HoleCutDiameter = 6.1
  HoleCutType = 1
  ModelThread = false
  Profile = -> Sketch015
  Reversed = true
  Suppressed = false
  Tapered = false
  TaperedAngle = 90
  ThreadClass = 0
  ThreadDepth = 15.822
  ThreadDepthType = 0
  ThreadDirection = 0
  ThreadFit = 0
  ThreadSize = 4
  ThreadType = 1
  Threaded = false
  UseCustomThreadClearance = false
FEATURE [PartDesign::SubShapeBinder] Binder011
  BindCopyOnChange = 0
  BindMode = 0
  ClaimChildren = false
  Context = -> Body003 [Binder011.]
  Fuse = false
  MakeFace = true
  OffsetFill = false
  OffsetIntersection = false
  OffsetJoinType = 0
  OffsetOpenResult = false
  PartialLoad = false
  Placement = pos=(25.9,0,0) rot=(0,0,1;0rad)
  Relative = true
  Support = -> [Sketch015]
  _Version = 2
FEATURE [PartDesign::Hole] Hole002
  BaseFeature = -> Hole001
  CustomThreadClearance = 0
  Depth = 5
  DepthType = 0
  Diameter = 1.6
  DrillForDepth = false
  DrillPoint = 1
  DrillPointAngle = 118
  HoleCutCountersinkAngle = 90
  HoleCutCustomValues = false
  HoleCutDepth = 1.2
  HoleCutDiameter = 6.1
  HoleCutType = 1
  ModelThread = false
  Profile = -> Binder011
  Suppressed = false
  Tapered = false
  TaperedAngle = 90
  ThreadClass = 0
  ThreadDepth = 5
  ThreadDepthType = 0
  ThreadDirection = 0
  ThreadFit = 0
  ThreadSize = 3
  ThreadType = 1
  Threaded = false
  UseCustomThreadClearance = false
FEATURE [PartDesign::Body] Body003  label="propguard"
  AllowCompound = false
  Group = -> [Sketch007,Binder007,Pad005,Sketch008,Pad006,Sketch009,Pad007,Binder008,PolarPattern,Plane001,Sketch015,Hole001,Binder011,Hole002]
  Origin = -> Origin006
  Tip = -> Hole002
